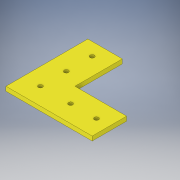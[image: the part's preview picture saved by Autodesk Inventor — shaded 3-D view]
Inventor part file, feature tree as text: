
AUTODESK INVENTOR PART (.ipt)
format: ipt  version: 2017 SP1 (Build 210196100, 196)  size: 109,056 bytes
history: native  units: in
note: dims shown in document units (in); Inventor stores cm internally (conversion verified against a paired STEP export)
features: extrude x1, sketch x1
ambient origin geometry x8: Origin, YZ Plane, XZ Plane, XY Plane, X Axis, Y Axis, Z Axis, Center Point
bodies: Solid1 (feature_tree)
feature tree (2):
  extrude  "Extrusion1"  Depth=0.875in
  sketch  "Sketch1"  dims[d0=0.125in d1=0.875in d2=1.0in d3=0.375in d4=0.75in d5=0.75in d6=0.125in d7=0.0in]
